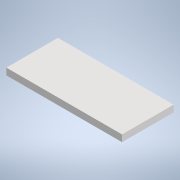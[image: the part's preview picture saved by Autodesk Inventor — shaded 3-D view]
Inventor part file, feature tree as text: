
AUTODESK INVENTOR PART (.ipt)
format: ipt  version: 2022 (Build 260153000, 153)  size: 89,600 bytes
history: native  units: mm
features: other x1, extrude x1, sketch x1
ambient origin geometry x8: Origin, YZ Plane, XZ Plane, XY Plane, X Axis, Y Axis, Z Axis, Center Point
bodies: Body1 (feature_tree)
feature tree (3):
  other  "Твердое тело1"
  extrude  "Выдавливание1"  Depth=52.0mm
  sketch  "Эскиз1"
